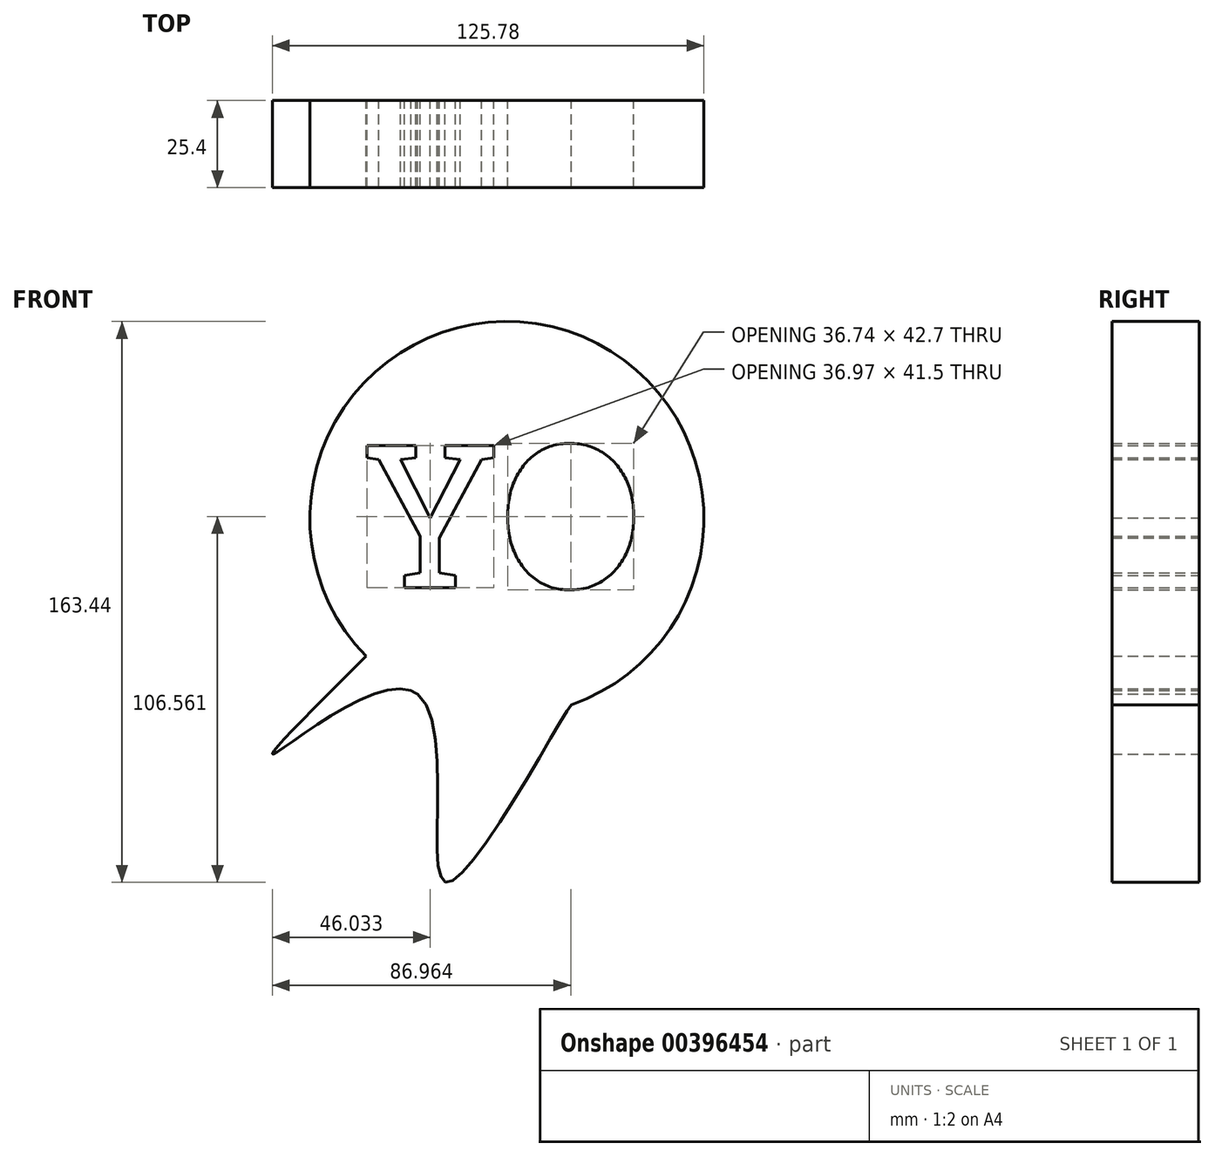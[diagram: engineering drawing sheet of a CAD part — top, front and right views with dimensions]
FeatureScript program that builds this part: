
annotation { "Feature Type Name" : "Feature", "Feature Type Description" : "" }
export const myFeature = defineFeature(function(context is Context, id is Id, definition is map)
    precondition{}
    {
        {
            var Q0;
            Q0=qCreatedBy(makeId("Front.planeOp"),FACE);
            var sketch = newSketch(context, id + "F0", { "sketchPlane" : qUnion([Q0])});
            skCircle(sketch, "E0", {"center": v(-0.87, 5.69) * mm, "radius": 57.42 * mm});
            skPoint(sketch, "E0.first.point", {"position": v(-49.9, 35.57) * mm});
            skPoint(sketch, "E0.second.point", {"position": v(42.14, -32.35) * mm});
            skPoint(sketch, "E0.third.point", {"position": v(-29.15, -44.28) * mm});
            skFitSpline(sketch, "E1", {"points": [v(-41.94, -34.44) * mm, v(-68.55, -62.79) * mm, v(-26.93, -45.48) * mm, v(-18.5, -100.3) * mm, v(17.94, -48.56) * mm, v(18.4, -48.4) * mm], "startDerivative": vector(-214.86, -213.3) * mm, "endDerivative": vector(12.55, -10.23) * mm});
            skText(sketch, "E2", { "text": "YO", "fontName": "RobotoSlab-Regular.ttf"});
            const initialGuessF0  = {"E2": [-0.04325, -0.01452, 1, 0, 0.04203]};
            skSetInitialGuess(sketch, initialGuessF0);
            skSolve(sketch);
        }
        {
            var Q0;
            Q0 = qSketchRegion(id + "F0", true);
            extrude(context, id + "F1", {"entities" : qUnion([Q0]), "depth" : 25.4 * mm});
        }
    });
